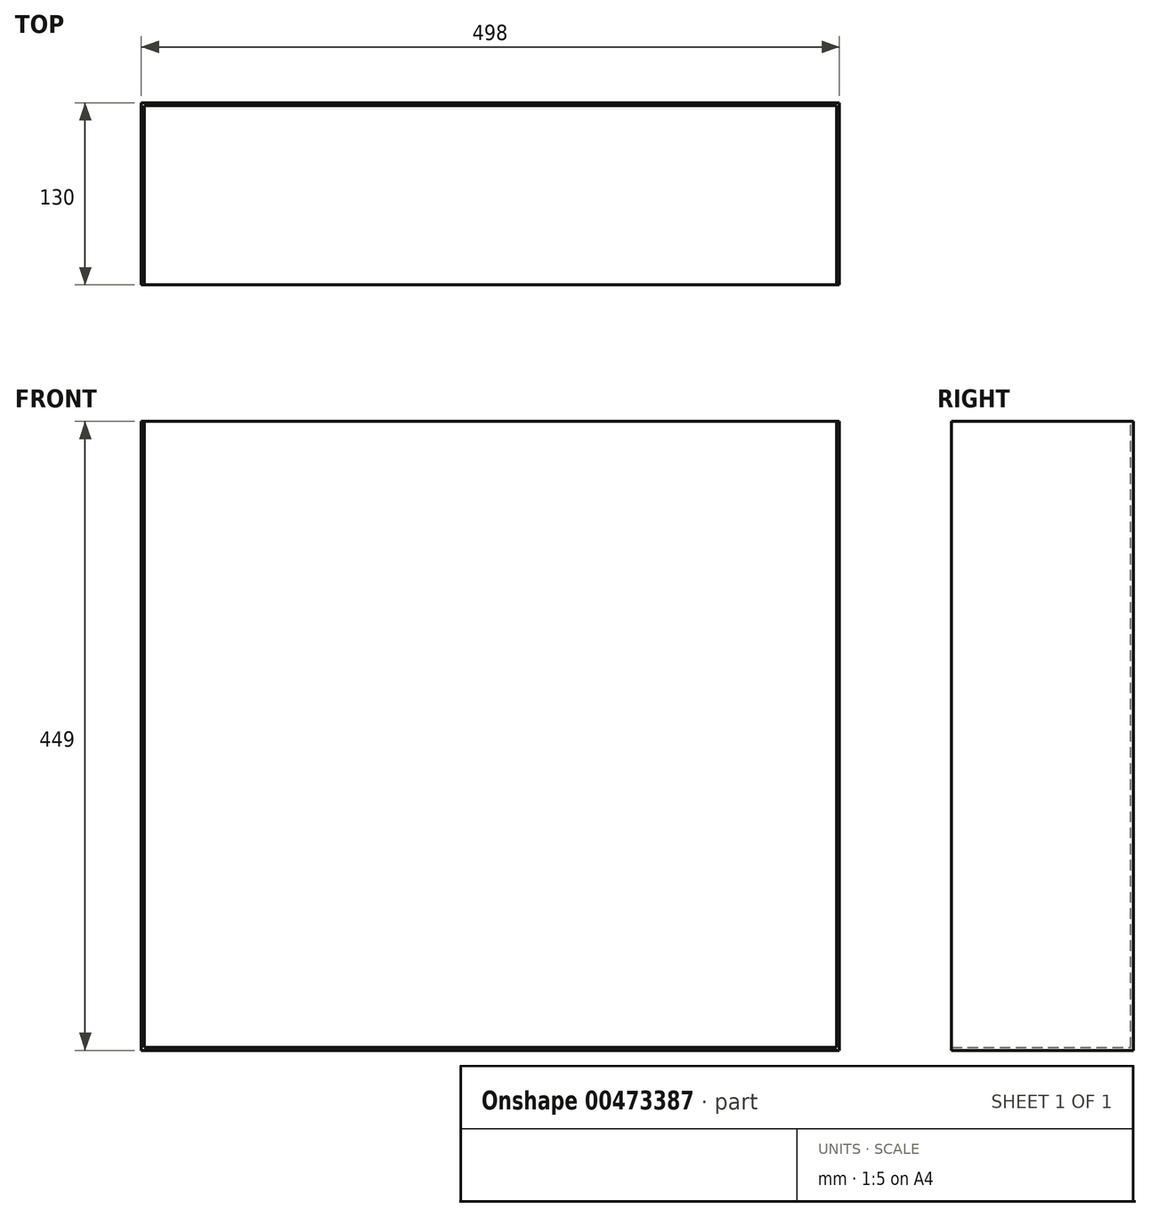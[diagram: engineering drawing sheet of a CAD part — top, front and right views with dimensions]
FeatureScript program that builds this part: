
annotation { "Feature Type Name" : "Feature", "Feature Type Description" : "" }
export const myFeature = defineFeature(function(context is Context, id is Id, definition is map)
    precondition{}
    {
        {
            var Q0;
            Q0=qCreatedBy(makeId("Top.planeOp"),FACE);
            var sketch = newSketch(context, id + "F0", { "sketchPlane" : qUnion([Q0])});
            skLineSegment(sketch, "E0.bottom", {"start": v(0, 0) * mm, "end": v(498, 0) * mm});
            skLineSegment(sketch, "E0.top", {"start": v(0, 130) * mm, "end": v(498, 130) * mm});
            skLineSegment(sketch, "E0.left", {"start": v(0, 0) * mm, "end": v(0, 130) * mm});
            skLineSegment(sketch, "E0.right", {"start": v(498, 0) * mm, "end": v(498, 130) * mm});
            skSolve(sketch);
        }
        {
            var Q0;
            Q0=qSketchRegion(id+"F0",true);
            extrude(context, id + "F1", {"entities" : qUnion([Q0]), "oppositeDirection" : true, "depth" : 449 * mm});
        }
        {
            var Q0;
            Q0=makeQuery(id+"F1.opExtrude","SWEPT_FACE",FACE,{"disambiguationData":[OSD([sQuery(id+"F0.wireOp",EDGE,"E0.bottom")])]});
            var Q1;
            Q1=makeQuery(id+"F1.opExtrude","CAP_FACE",FACE,{"disambiguationData":[OSD([sQuery(id+"F0.wireOp",EDGE,"E0.bottom"),sQuery(id+"F0.wireOp",EDGE,"E0.top"),sQuery(id+"F0.wireOp",EDGE,"E0.left"),sQuery(id+"F0.wireOp",EDGE,"E0.right")])],"isStart":true});
            shell(context, id + "F2", {"entities" : qUnion([Q0, Q1]), "thickness" : 2 * mm});
        }
    });
